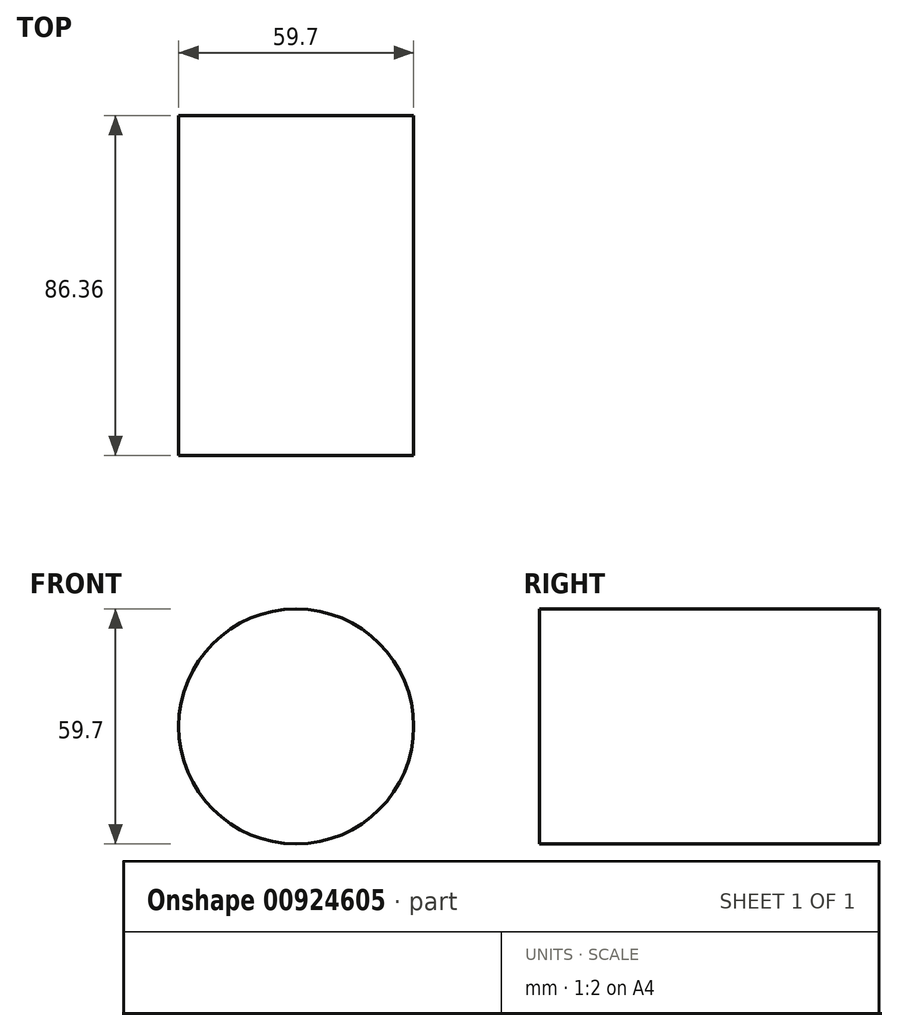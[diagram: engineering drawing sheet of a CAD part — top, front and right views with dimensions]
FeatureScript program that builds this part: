
annotation { "Feature Type Name" : "Feature", "Feature Type Description" : "" }
export const myFeature = defineFeature(function(context is Context, id is Id, definition is map)
    precondition{}
    {
        {
            var Q0;
            Q0=qCreatedBy(makeId("Front.planeOp"),FACE);
            var sketch = newSketch(context, id + "F0", { "sketchPlane" : qUnion([Q0])});
            skCircle(sketch, "E0", {"center": v(-112.62, 13.9) * mm, "radius": 29.85 * mm});
            skSolve(sketch);
        }
        {
            var Q0;
            Q0 = qSketchRegion(id + "F0", true);
            extrude(context, id + "F1", {"entities" : qUnion([Q0]), "depth" : 86.36 * mm, "offsetDistance" : 25.4 * mm});
        }
    });
